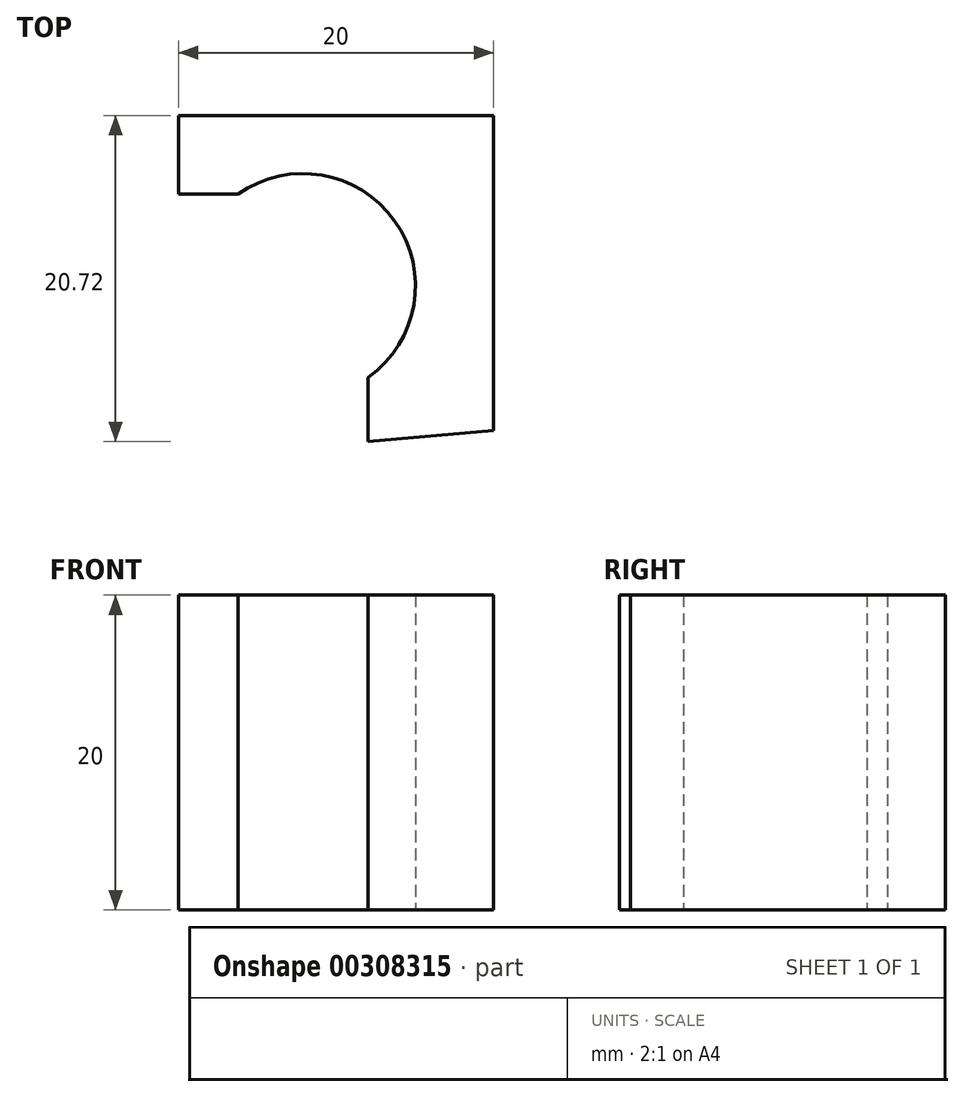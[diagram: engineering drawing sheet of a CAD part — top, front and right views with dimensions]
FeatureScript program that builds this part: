
annotation { "Feature Type Name" : "Feature", "Feature Type Description" : "" }
export const myFeature = defineFeature(function(context is Context, id is Id, definition is map)
    precondition{}
    {
        {
            var Q0;
            Q0=qCreatedBy(makeId("Top.planeOp"),FACE);
            var sketch = newSketch(context, id + "F0", { "sketchPlane" : qUnion([Q0])});
            skLineSegment(sketch, "E0", {"start": v(36.58, 44.27) * mm, "end": v(56.58, 44.27) * mm});
            skLineSegment(sketch, "E1", {"start": v(56.58, 44.27) * mm, "end": v(56.58, 24.27) * mm});
            skLineSegment(sketch, "E2", {"start": v(56.58, 24.27) * mm, "end": v(48.62, 23.55) * mm});
            skLineSegment(sketch, "E3", {"start": v(48.62, 23.55) * mm, "end": v(48.62, 27.63) * mm});
            skArc(sketch, "E4", {"start": v(48.62, 27.63) * mm, "mid": v(50.3, 37.57) * mm, "end": v(40.36, 39.27) * mm});
            skLineSegment(sketch, "E5", {"start": v(40.36, 39.27) * mm, "end": v(36.58, 39.27) * mm});
            skLineSegment(sketch, "E6", {"start": v(36.58, 39.27) * mm, "end": v(36.58, 44.27) * mm});
            skSolve(sketch);
        }
        {
            var Q0;
            Q0=makeQuery(id+"F0.imprint","IMPRINT",FACE,{"disambiguationData":[TD([[makeQuery(id+"F0.imprint","IMPRINT",EDGE,{"derivedFrom":sQuery(id+"F0.wireOp",EDGE,"E0")}),-1.0]])]});
            extrude(context, id + "F1", {"entities" : qUnion([Q0]), "depth" : 20 * mm});
        }
    });
